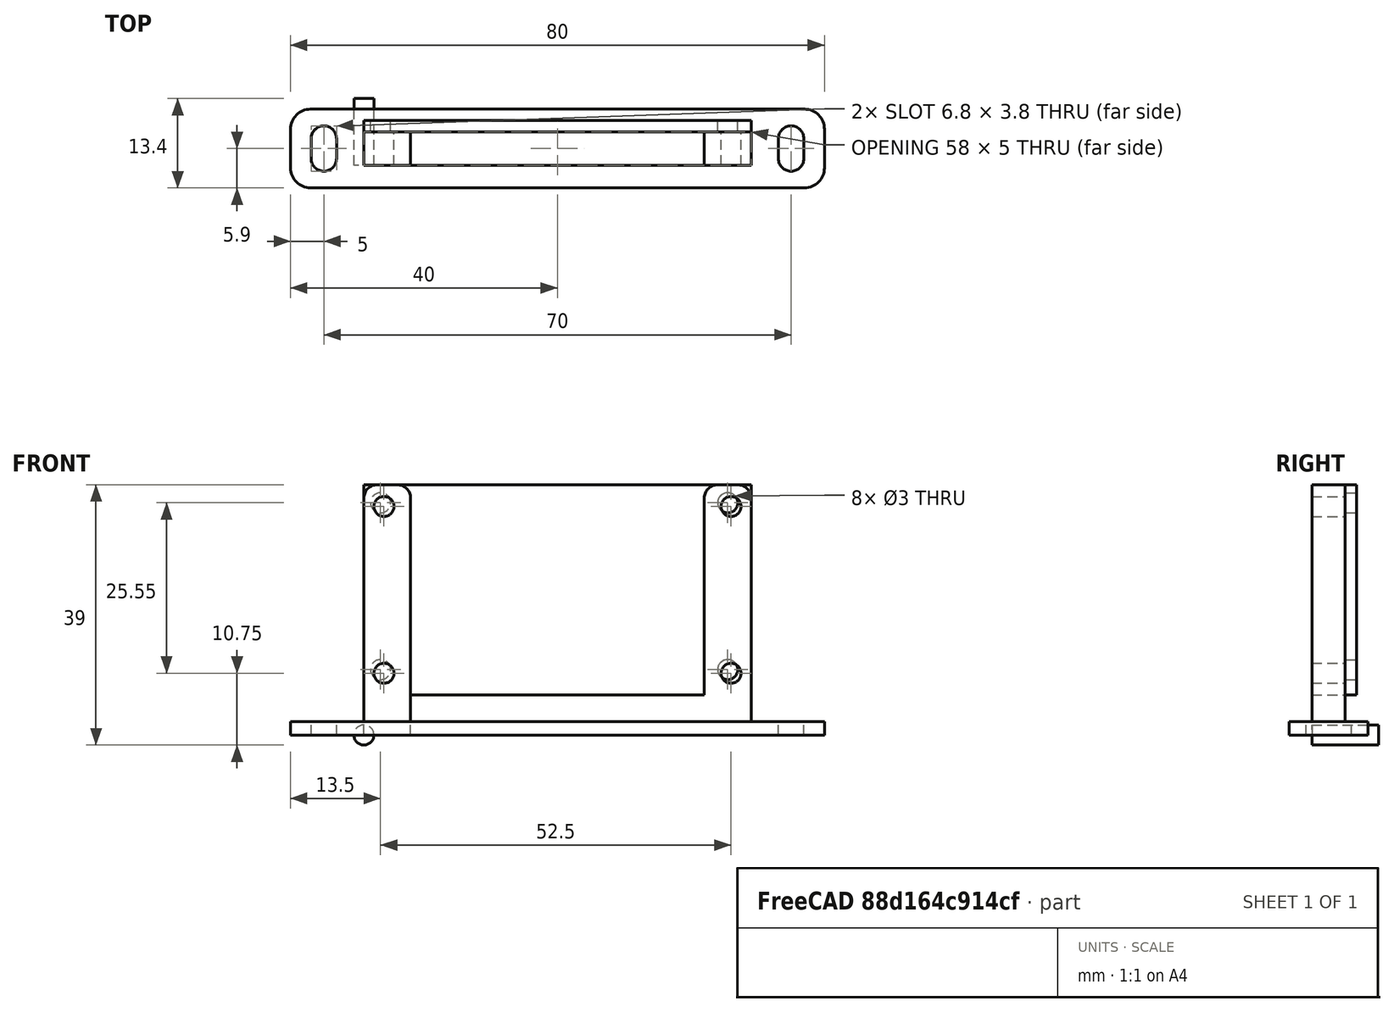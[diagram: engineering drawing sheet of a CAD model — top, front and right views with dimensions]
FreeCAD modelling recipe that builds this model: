
FCSTD DOCUMENT  (FreeCAD 0.19R23578 (Git))
Label: esp8266_bigger
License: All rights reserved
LicenseURL: http://en.wikipedia.org/wiki/All_rights_reserved
objects: Part::Box×3, Part::FeaturePython×2, Part::Cut×2, Spreadsheet::Sheet×1, Part::Cylinder×1, Part::Fillet×1, PartDesign::FeatureBase×1, PartDesign::Body×1, Part::Feature×1, Part::MultiFuse×1
note: 11 computed .brp shape members not serialized (recipe doc carries the construction recipe); baked Part::Feature solids carry a one-line shape summary decoded from their .brp

FEATURE [Part::Box] Box  label="v attachment"
  AttacherType = Attacher::AttachEngine3D
  Height = 37.5
  Length = 7
  Width = 5
  expr: Length = <<p>>.hole_stand_length
  expr: Width = <<p>>.thickness
  expr: Height = <<p>>.pcb_width + <<p>>.bottom_offset
FEATURE [Spreadsheet::Sheet] Spreadsheet  label="p"
  cells = A1=pcb_length; B1(pcb_length)=58; A2=pcb_width; B2(pcb_width)=31.5; A3=pcb_height; B3(pcb_height)=1.7; A4=hole_dist_length; B4(hole_dist_length)=52; A5=hole_dist_width; B5(hole_dist_width)=25; A6=hole_r; B6(hole_r)=1.5; A7=thickness; B7(thickness)=5; A8=bottom_offset; B8(bottom_offset)=6; A9=hole_stand_length; B9(hole_stand_length)=7
FEATURE [Part::Box] Box001  label="bottom block"
  AttacherType = Attacher::AttachEngine3D
  Height = 6
  Length = 58
  Width = 5
  expr: Height = <<p>>.bottom_offset
  expr: Width = <<p>>.thickness
  expr: Length = <<p>>.pcb_length
FEATURE [Part::Box] Box002  label="pcb mockup body"
  AttacherType = Attacher::AttachEngine3D
  Height = 31.5
  Length = 58
  Placement = pos=(0,5,6) rot=(0,0,1;0rad)
  Width = 1.7
  expr: Length = <<p>>.pcb_length
  expr: Width = <<p>>.pcb_height
  expr: Height = <<p>>.pcb_width
  expr: .Placement.Base.z = <<p>>.bottom_offset
  expr: .Placement.Base.y = <<p>>.thickness
FEATURE [Part::Cylinder] Cylinder  label="hole"
  Angle = 360
  AttacherType = Attacher::AttachEngine3D
  Height = 10
  Placement = pos=(0,0,0) rot=(-1,0,0;1.5708rad)
  Radius = 1.5
  expr: Radius = <<p>>.hole_r
FEATURE [Part::FeaturePython] Array001  label="hole array"  # Draft array (typed FeaturePython)
  Angle = 360
  ArrayType = 0
  Axis = (0,0,1)
  Base = -> Cylinder
  Center = (0,0,0)
  Count = 4
  ExpandArray = false
  Fuse = false
  IntervalAxis = (0,0,0)
  IntervalX = (52,0,0)
  IntervalY = (0,100,0)
  IntervalZ = (0,0,25)
  NumberCircles = 3
  NumberPolar = 5
  NumberX = 2
  NumberY = 1
  NumberZ = 2
  Placement = pos=(3,0,9.25) rot=(0,0,1;0rad)
  PlacementList = 4 placements: [(0,0,0),(0,0,25),(52,0,0),(52,0,25)]
  RadialDistance = 50
  ScaleList = (4) [(1,1,1),(1,1,1),(1,1,1),(1,1,1)]
  Symmetry = 1
  TangentialDistance = 25
  expr: .IntervalX.x = <<p>>.hole_dist_length
  expr: .IntervalZ.z = <<p>>.hole_dist_width
  expr: .Placement.Base.z = <<p>>.bottom_offset + (<<p>>.pcb_width - <<p>>.hole_dist_width) / 2
  expr: .Placement.Base.x = (<<p>>.pcb_length - <<p>>.hole_dist_length) / 2
FEATURE [Part::Fillet] Fillet  label="v attachment fillet"
  Base = -> Box
  Edges = 2 edges r=2: [Edge2,Edge6]
FEATURE [Part::FeaturePython] Array  label="v attachment array"  # Draft array (typed FeaturePython)
  Angle = 360
  ArrayType = 0
  Axis = (0,0,1)
  Base = -> Fillet
  Center = (0,0,0)
  Count = 2
  ExpandArray = false
  Fuse = false
  IntervalAxis = (0,0,0)
  IntervalX = (51,0,0)
  IntervalY = (0,1,0)
  IntervalZ = (0,0,100)
  NumberCircles = 3
  NumberPolar = 5
  NumberX = 2
  NumberY = 1
  NumberZ = 1
  PlacementList = 2 placements: [(0,0,0),(51,0,0)]
  RadialDistance = 50
  ScaleList = (2) [(1,1,1),(1,1,1)]
  Symmetry = 1
  TangentialDistance = 25
  expr: .IntervalX.x = <<p>>.pcb_length - <<p>>.hole_stand_length
FEATURE [Part::Cut] Cut001  label="attachment cut"
  Base = -> Array
  Tool = -> Array001
FEATURE [PartDesign::FeatureBase] Clone001
  BaseFeature = -> Array001
  Placement = pos=(2.5,0,9.8) rot=(0,0,1;0rad)
FEATURE [PartDesign::Body] Body001  label="hole array clone"
  BaseFeature = -> Array001
  Group = -> [Clone001]
  Origin = -> Origin001
  Tip = -> Clone001
FEATURE [Part::Cut] Cut  label="pcb mockup"
  Base = -> Box002
  Tool = -> Body001
FEATURE [Part::Feature] Cut003002  label="attach plane x dir002"
  Placement = pos=(-11,-3.4,0) rot=(0,0,1;0rad)
  shape: bbox 80 x 11.8 x 2 mm, 18 faces (baked)
FEATURE [Part::MultiFuse] Fusion  label="pcb attachment fusion"
  Shapes = -> [Box001,Cut001,Cut003002]
